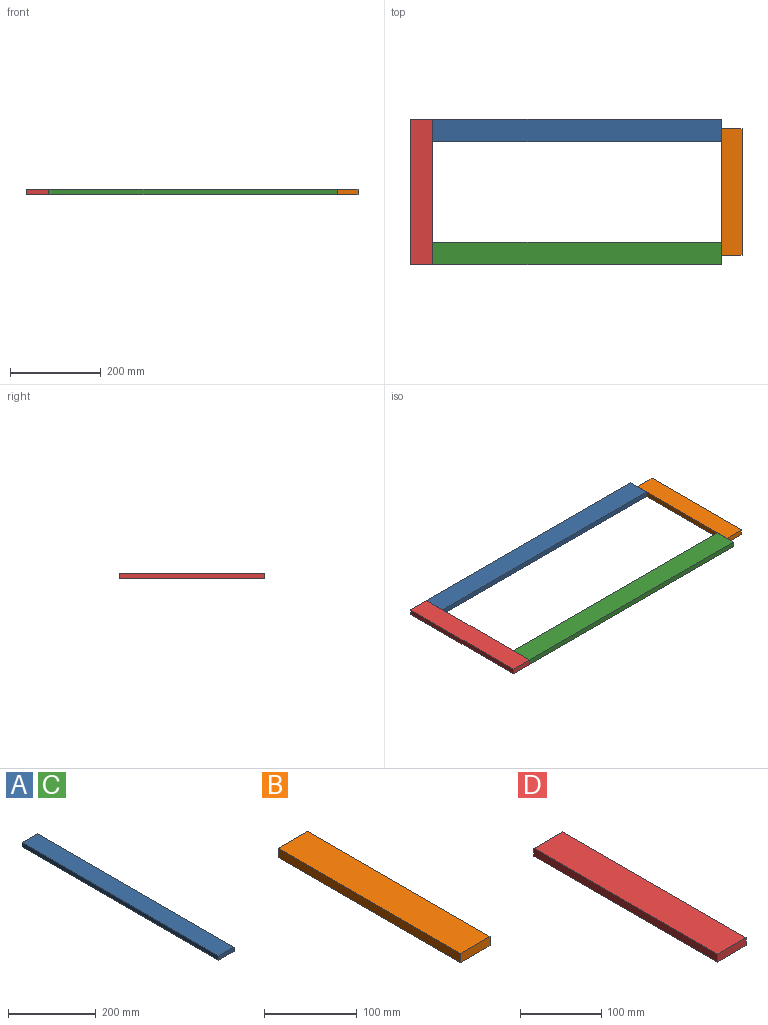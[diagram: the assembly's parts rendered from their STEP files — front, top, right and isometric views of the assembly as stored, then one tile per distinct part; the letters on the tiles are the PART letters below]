
ASSEMBLY  parts=4 mates=3
PART A: 6 faces, bbox 50x635x12 mm
  f0: plane 635x12mm, normal (1,0,0), area 7620mm2, adj f1,f3,f4,f5
  f1: plane 635x50mm, normal (0,0,1), area 31750mm2, adj f0,f2,f4,f5
  f2: plane 635x12mm, normal (-1,0,0), area 7620mm2, adj f1,f3,f4,f5
  f3: plane 635x50mm, normal (0,0,-1), area 31750mm2, adj f0,f2,f4,f5
  f4: plane 50x12mm, normal (0,1,0), area 600mm2, adj f0,f1,f2,f3
  f5: plane 50x12mm, normal (0,-1,0), area 600mm2, adj f0,f1,f2,f3
PART B: 6 faces, bbox 45x278x12 mm
  f0: plane 278x12mm, normal (1,0,0), area 3336mm2, adj f1,f3,f4,f5
  f1: plane 278x45mm, normal (0,0,1), area 12510mm2, adj f0,f2,f4,f5
  f2: plane 278x12mm, normal (-1,0,0), area 3336mm2, adj f1,f3,f4,f5
  f3: plane 278x45mm, normal (0,0,-1), area 12510mm2, adj f0,f2,f4,f5
  f4: plane 45x12mm, normal (0,1,0), area 540mm2, adj f0,f1,f2,f3
  f5: plane 45x12mm, normal (0,-1,0), area 540mm2, adj f0,f1,f2,f3
PART C: same geometry as A
PART D: 6 faces, bbox 50x320x12 mm
  f0: plane 320x12mm, normal (1,0,0), area 3840mm2, adj f1,f3,f4,f5
  f1: plane 320x50mm, normal (0,0,1), area 16000mm2, adj f0,f2,f4,f5
  f2: plane 320x12mm, normal (-1,0,0), area 3840mm2, adj f1,f3,f4,f5
  f3: plane 320x50mm, normal (0,0,-1), area 16000mm2, adj f0,f2,f4,f5
  f4: plane 50x12mm, normal (0,1,0), area 600mm2, adj f0,f1,f2,f3
  f5: plane 50x12mm, normal (0,-1,0), area 600mm2, adj f0,f1,f2,f3
PLACE A rot(axis=(0,0,1),90deg) t=(111.69,346.42,125.73)mm
PLACE B t=(134.19,72.42,125.73)mm
PLACE C rot(axis=(0,0,1),90deg) t=(111.69,76.42,125.73)mm
PLACE D t=(-548.31,51.42,125.73)mm
MATE fastened D.f1 <-> A.f1  axis (0,0,1) through (-523.31,371.42,131.73)mm
MATE fastened D.f3 <-> C.f3  axis (0,0,1) through (-523.31,51.42,119.73)mm
MATE fastened C.f3 <-> B.f3  axis (0,0,1) through (111.69,51.42,119.73)mm
